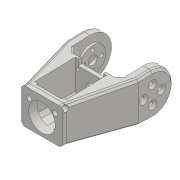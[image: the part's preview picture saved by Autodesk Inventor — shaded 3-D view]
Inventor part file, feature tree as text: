
AUTODESK INVENTOR PART (.ipt)
format: ipt  version: 2018 (Build 220112000, 112)  size: 1,031,680 bytes
history: native  units: mm
features: sketch x39, extrude x34, projected_geometry x33, hole x10, fillet x10, chamfer x10, mirror x1, plane x1
ambient origin geometry x8: Origin, YZ Plane, XZ Plane, XY Plane, X Axis, Y Axis, Z Axis, Center Point
bodies: Solid1 (feature_tree)
feature tree (138):
  extrude  "Extrusion1"  Depth=45.0mm
  extrude  "Extrusion2"  Depth=2.25mm
  hole  "Hole1"  [1 undecoded]
  hole  "Hole2"  [1 undecoded]
  fillet  "Fillet1"  Radius=14.0mm
  extrude  "Extrusion3"  Depth=18.5mm
  extrude  "Extrusion4"  Depth=10.0mm
  extrude  "Extrusion5"  Depth=2.195mm
  extrude  "Extrusion6"  Depth=20.5mm
  hole  "Hole3"  [1 undecoded]
  extrude  "Extrusion7"  Depth=0.5mm
  extrude  "Extrusion8"  Depth=5.0mm TaperAngle=0.0deg
  extrude  "Extrusion9"  Depth=10.0mm
  extrude  "Extrusion10"  Depth=10.0mm
  extrude  "Extrusion11"  Depth=14.5mm
  extrude  "Extrusion12"  Depth=14.5mm
  extrude  "Extrusion13"  Depth=5.0mm
  extrude  "Extrusion14"  Depth=2.25mm
  extrude  "Extrusion15"  Depth=5.0mm
  extrude  "Extrusion16"  Depth=9.0mm
  extrude  "Extrusion17"  Depth=4.0mm
  chamfer  "Chamfer1"  Distance=1.0mm
  fillet  "Fillet7"  Radius=20.7mm
  fillet  "Fillet8"  Radius=32.0mm
  mirror  "Mirror1"
  extrude  "Extrusion19"  Depth=1.0mm TaperAngle=0.0deg
  extrude  "Extrusion20"  Depth=8.0mm
  extrude  "Extrusion21"  Depth=0.2mm TaperAngle=0.0deg
  extrude  "Extrusion22"  Depth=0.5mm TaperAngle=0.0deg
  sketch  "Sketch29"  dims[d77=12.25mm d78=0.0mm d80=8.0mm]
  extrude  "Extrusion23"  Depth=5.0mm TaperAngle=0.0deg
  extrude  "Extrusion24"  Depth=0.2mm TaperAngle=0.0deg
  plane  "Work Plane1"
  extrude  "Extrusion25"  Depth=2.5mm TaperAngle=45.0deg
  extrude  "Extrusion26"  Depth=0.5mm
  extrude  "Extrusion27"  Depth=8.0mm
  extrude  "Extrusion28"  Depth=3.0mm TaperAngle=0.0deg
  extrude  "Extrusion29"  Depth=33.0mm
  extrude  "Extrusion30"  Depth=56.0mm
  extrude  "Extrusion31"  Depth=25.0mm TaperAngle=0.0deg
  chamfer  "Chamfer2"  Distance=6.0mm
  hole  "Hole6"  [1 undecoded]
  chamfer  "Chamfer3"  Distance=4.5mm
  extrude  "Extrusion32"  Depth=1.8mm TaperAngle=0.0deg
  extrude  "Extrusion33"  Depth=1.8mm
  chamfer  "Chamfer4"  Distance=12.0mm
  chamfer  "Chamfer5"  Distance=12.0mm
  chamfer  "Chamfer6"  Distance=40.0mm
  fillet  "Fillet9"  Radius=40.0mm
  extrude  "Extrusion34"  Depth=1.8mm
  chamfer  "Chamfer7"  Distance=1.8mm
  sketch  "Sketch42"  dims[d146=6.0mm d147=0.0mm d149=42.0mm]
  hole  "Hole7"  [1 undecoded]
  hole  "Hole8"  [1 undecoded]
  hole  "Hole9"  [1 undecoded]
  fillet  "Fillet10"  Radius=14.0mm
  chamfer  "Chamfer8"  Distance=1.2mm Angle=45.0deg
  chamfer  "Chamfer9"  Distance=7.0mm
  fillet  "Fillet11"  Radius=2.5mm
  fillet  "Fillet12"  Radius=7.0mm
  extrude  "Extrusion35"  Depth=1.8mm TaperAngle=0.0deg
  sketch  "Sketch45"  dims[d151=4.5mm d152=4.5mm d153=40.0mm d154=0.0mm d155=28.0mm d156=12.0mm d157=12.0mm d158=40.0mm d159=0.0mm d160=40.0mm d161=0.0mm d162=20.5mm d163=1.8mm d164=0.0mm d165=20.5mm d166=3.3mm d167=0.0mm d168=2.0mm d169=2.0mm d170=45.0deg d171=14.0mm d172=3.1mm d173=6.0mm d174=6.3mm d175=2.0mm d176=90.0deg d177=8.0mm d178=20.594885mm d179=1.2mm d180=2.0mm d181=45.0deg d182=7.0mm d183=2.5mm d184=0.0mm d185=7.0mm d186=2.5mm d187=0.0mm d188=3.0mm d189=15.0mm d190=45.0deg d191=3.0mm d192=15.0mm d193=45.0deg d194=3.0mm d195=15.0mm d196=45.0deg d197=2.0mm d198=12.0mm d199=2.0mm d200=15.0mm d201=20.0mm d202=0.0mm d203=2.0mm d204=15.0mm d205=45.0deg d206=2.9mm d207=2.9mm d208=3.18mm d209=3.18mm d210=4.0mm d211=6.0mm d212=6.3mm d213=2.0mm d214=90.0deg d215=8.0mm d216=20.594885mm d217=1.567mm d218=25.0mm d219=6.3mm d220=2.0mm d221=90.0deg d222=25.0mm d223=20.594885mm d224=2.15mm d225=20.0mm d226=4.4mm d227=2.0mm d228=90.0deg d229=10.0mm d230=0.0mm d231=0.5mm d232=2.0mm d233=15.0mm d234=45.0deg d235=2.0mm d236=15.0mm d237=45.0deg d238=1.0mm d239=3.0mm d240=3.9mm d241=3.9mm d242=3.5mm d243=0.0mm d244=2.75mm d245=2.75mm d246=2.5mm d247=1.567mm d248=4.0mm d249=4.4mm d250=2.0mm d251=90.0deg d252=40.0mm d253=20.594885mm d254=2.1mm d255=4.0mm d256=4.4mm d257=2.0mm d258=90.0deg d259=28.25mm d260=0.0mm d261=3.9mm d262=4.0mm d263=4.4mm d264=2.0mm d265=90.0deg d266=20.0mm d267=0.0mm d268=0.2mm d269=2.0mm d270=2.0mm d271=1.8mm d272=15.0mm d273=45.0deg]
  hole  "Hole10"  [1 undecoded]
  hole  "Hole11"  [1 undecoded]
  hole  "Hole12"  [1 undecoded]
  fillet  "Fillet13"  Radius=2.0mm
  fillet  "Fillet14"  Radius=12.0mm
  fillet  "Fillet15"  Radius=2.0mm
  chamfer  "Chamfer10"  Distance=15.0mm
  sketch  "Sketch1"  dims[d0=24.5mm d1=45.0mm]
  sketch  "Sketch2"  dims[d2=1.95mm d3=0.0mm d4=2.25mm]
  projected_geometry  "Projected Loop1"
  sketch  "Sketch3"  dims[d5=20.0mm d6=2.25mm]
  projected_geometry  "Projected Loop2"
  sketch  "Sketch4"  dims[d7=5.25mm d8=5.25mm d9=14.0mm]
  projected_geometry  "Projected Loop3"
  sketch  "Sketch5"  dims[d10=5.25mm d11=18.5mm]
  projected_geometry  "Projected Loop4"
  sketch  "Sketch6"  dims[d12=10.0mm d13=0.0mm d14=20.5mm]
  projected_geometry  "Projected Loop5"
  sketch  "Sketch7"  dims[d15=2.0mm d16=2.195mm]
  projected_geometry  "Projected Loop6"
  sketch  "Sketch8"  dims[d17=2.0mm]
  projected_geometry  "Projected Loop7"
  sketch  "Sketch9"  dims[d18=2.4mm d19=6.0mm d20=4.4mm d21=2.0mm d22=90.0deg d23=8.0mm d24=20.594885mm d25=20.5mm]
  projected_geometry  "Projected Loop8"
  projected_geometry  "Projected Loop9"
  sketch  "Sketch10"  dims[d26=26.65mm d27=2.0mm]
  projected_geometry  "Projected Loop10"
  projected_geometry  "Projected Loop11"
  sketch  "Sketch11"  dims[d28=2.0mm]
  projected_geometry  "Projected Loop12"
  sketch  "Sketch12"  dims[d29=2.4mm d30=6.0mm d31=4.4mm d32=2.0mm d33=90.0deg d34=8.0mm d35=20.594885mm d36=0.5mm]
  sketch  "Sketch13"  dims[d37=18.0mm d38=5.0mm d39=0.0mm]
  sketch  "Sketch14"  dims[d41=10.0mm d42=0.0mm d43=24.5mm]
  projected_geometry  "Projected Loop13"
  sketch  "Sketch15"  dims[d44=1.15mm d45=0.0mm d46=10.0mm]
  sketch  "Sketch16"  dims[d47=21.0mm d48=14.5mm]
  projected_geometry  "Projected Loop14"
  sketch  "Sketch17"  dims[d49=20.0mm d50=14.5mm]
  projected_geometry  "Projected Loop15"
  sketch  "Sketch18"  dims[d51=24.5mm d52=5.0mm]
  projected_geometry  "Projected Loop16"
  sketch  "Sketch19"  dims[d53=5.0mm d54=2.25mm]
  projected_geometry  "Projected Loop17"
  sketch  "Sketch20"  dims[d55=2.25mm d56=5.0mm]
  projected_geometry  "Projected Loop18"
  sketch  "Sketch25"  dims[d57=5.0mm d58=9.0mm]
  projected_geometry  "Projected Loop22"
  sketch  "Sketch26"  dims[d59=14.75mm d60=4.0mm d61=1.0mm d62=0.0mm d63=20.7mm]
  sketch  "Sketch27"  dims[d64=2.4mm d65=6.0mm d66=4.4mm d67=2.0mm d68=90.0deg d69=8.0mm d70=20.594885mm d72=32.0mm]
  projected_geometry  "Projected Loop23"
  sketch  "Sketch28"  dims[d73=5.0mm d74=0.0mm d75=1.0mm d76=0.0mm]
  projected_geometry  "Projected Loop24"
  sketch  "Sketch31"  dims[d81=4.5mm d82=0.0mm d84=0.2mm d85=0.0mm]
  projected_geometry  "Projected Loop25"
  sketch  "Sketch32"  dims[d86=21.0mm d87=0.5mm d88=0.0mm]
  projected_geometry  "Projected Loop26"
  sketch  "Sketch33"  dims[d91=8.0mm d92=0.0mm d93=5.0mm d94=0.0mm]
  sketch  "Sketch34"  dims[d95=5.0mm d96=0.0mm d98=0.2mm d99=0.0mm]
  sketch  "Sketch35"  dims[d100=0.2mm d101=0.0mm d102=2.5mm d103=2.0mm d104=45.0deg]
  projected_geometry  "Projected Loop27"
  sketch  "Sketch36"  dims[d105=1.5mm d114=0.5mm]
  sketch  "Sketch37"  dims[d128=4.0mm d129=0.0mm d130=8.0mm]
  sketch  "Sketch38"  dims[d131=3.0mm d132=0.0mm d133=3.0mm d134=0.0mm]
  projected_geometry  "Projected Loop28"
  sketch  "Sketch39"  dims[d135=25.0mm d136=0.0mm d137=33.0mm]
  projected_geometry  "Projected Loop29"
  sketch  "Sketch40"  dims[d138=2.5mm d139=56.0mm]
  projected_geometry  "Projected Loop30"
  sketch  "Sketch41"  dims[d140=25.0mm d141=0.0mm d142=25.0mm d143=0.0mm d144=6.0mm d145=0.0mm]
  sketch  "Sketch44"  dims[d150=4.5mm]
  projected_geometry  "Projected Loop31"
  projected_geometry  "Projected Loop32"
  projected_geometry  "Projected Loop33"
  projected_geometry  "Project Cut Edges1"
  projected_geometry  "Project Cut Edges2"
  projected_geometry  "Project Cut Edges3"
note: 10 required parameter values undecoded (feature->parameter linkage not recoverable at this tier; creation-order binding heuristic only, values carry confidence <= 0.55)
